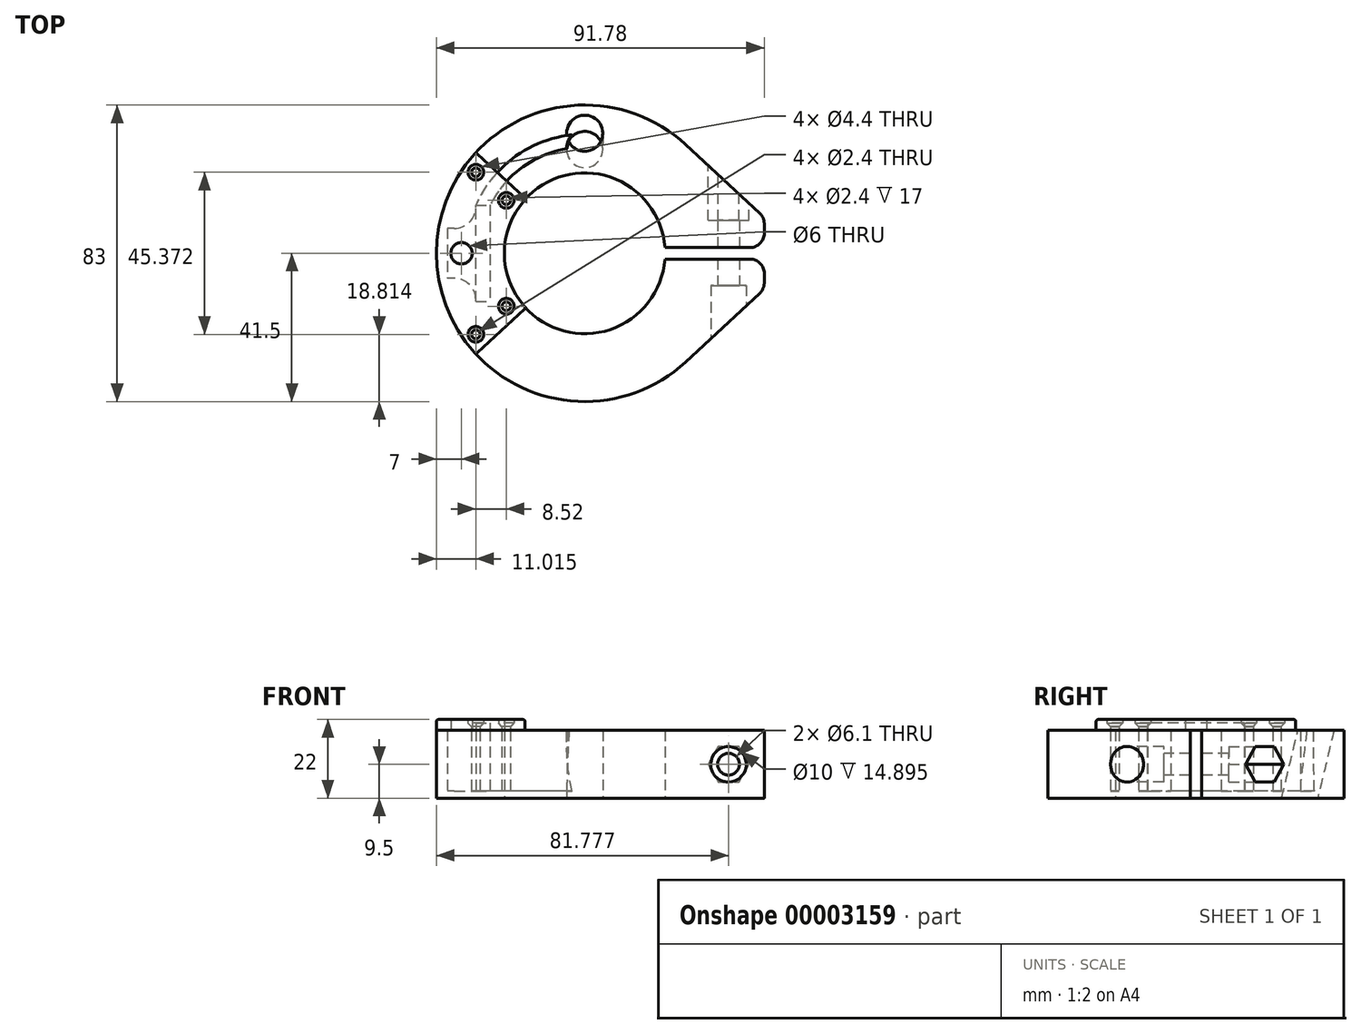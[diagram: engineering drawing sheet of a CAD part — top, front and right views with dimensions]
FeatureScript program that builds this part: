
annotation { "Feature Type Name" : "Feature", "Feature Type Description" : "" }
export const myFeature = defineFeature(function(context is Context, id is Id, definition is map)
    precondition{}
    {
        {
            var Q0;
            Q0=qCreatedBy(makeId("Top.planeOp"),FACE);
            var sketch = newSketch(context, id + "F0", { "sketchPlane" : qUnion([Q0])});
            skCircle(sketch, "E0", {"center": v(0, 0) * mm, "radius": 26.5 * mm, "construction": true});
            skCircle(sketch, "E1", {"center": v(0, 0) * mm, "radius": 38 * mm, "construction": true});
            skLineSegment(sketch, "E2", {"start": v(50.28, 1.6) * mm, "end": v(0, 1.6) * mm});
            skLineSegment(sketch, "E3", {"start": v(0, 1.6) * mm, "end": v(0, -1.6) * mm});
            skLineSegment(sketch, "E4", {"start": v(0, -1.6) * mm, "end": v(50.28, -1.6) * mm});
            skLineSegment(sketch, "E5", {"start": v(40.28, 10) * mm, "end": v(50.28, 10) * mm});
            skLineSegment(sketch, "E6", {"start": v(50.28, 10) * mm, "end": v(50.28, -10) * mm});
            skLineSegment(sketch, "E7", {"start": v(50.28, -10) * mm, "end": v(40.28, -10) * mm});
            skLineSegment(sketch, "E8", {"start": v(-26.5, 13.5) * mm, "end": v(-26.5, -13.5) * mm});
            skLineSegment(sketch, "E9", {"start": v(-30.5, -13.5) * mm, "end": v(-30.5, 13.5) * mm});
            skCircle(sketch, "E10", {"center": v(-34.5, 0) * mm, "radius": 3 * mm});
            skLineSegment(sketch, "E11", {"start": v(-30.5, 0) * mm, "end": v(-26.5, 0) * mm, "construction": true});
            skCircle(sketch, "E12", {"center": v(0, 0) * mm, "radius": 41.5 * mm});
            skLineSegment(sketch, "E13", {"start": v(-30.5, -13.5) * mm, "end": v(-26.5, -13.5) * mm});
            skLineSegment(sketch, "E14", {"start": v(-30.5, 13.5) * mm, "end": v(-26.5, 13.5) * mm});
            skLineSegment(sketch, "E15.rect.bottom", {"start": v(-30.5, 7) * mm, "end": v(-38.5, 7) * mm});
            skLineSegment(sketch, "E15.rect.top", {"start": v(-30.5, -7) * mm, "end": v(-38.5, -7) * mm});
            skLineSegment(sketch, "E15.rect.left", {"start": v(-30.5, 7) * mm, "end": v(-30.5, -7) * mm});
            skLineSegment(sketch, "E15.rect.right", {"start": v(-38.5, 7) * mm, "end": v(-38.5, -7) * mm});
            skCircle(sketch, "E16", {"center": v(0, 28.48) * mm, "radius": 5.05 * mm});
            skLineSegment(sketch, "E17", {"start": v(0, 26.5) * mm, "end": v(0, 41.5) * mm});
            skCircle(sketch, "E18", {"center": v(0, 0) * mm, "radius": 22.5 * mm});
            skLineSegment(sketch, "E19", {"start": v(-26.5, 0) * mm, "end": v(-22.5, 0) * mm});
            skLineSegment(sketch, "E20", {"start": v(0, 0) * mm, "end": v(50.28, 0) * mm, "construction": true});
            skArc(sketch, "E21", {"start": v(-1.43, 33.32) * mm, "mid": v(-18.8, 27.56) * mm, "end": v(-30.5, 13.5) * mm});
            skLineSegment(sketch, "E22", {"start": v(-16.54, 15.26) * mm, "end": v(-30.5, 28.14) * mm});
            skLineSegment(sketch, "E23", {"start": v(-30.5, -28.14) * mm, "end": v(-16.54, -15.26) * mm});
            skLineSegment(sketch, "E24", {"start": v(-30.5, 28.14) * mm, "end": v(-30.5, -28.14) * mm, "construction": true});
            skArc(sketch, "E25.trimOffspring", {"start": v(-4.98, 29.32) * mm, "mid": v(-17.62, 23.96) * mm, "end": v(-26.5, 13.5) * mm});
            skLineSegment(sketch, "E26.0", {"start": v(-33.07, -25.07) * mm, "end": v(-18.99, -12.08) * mm, "construction": true});
            skLineSegment(sketch, "E27.0", {"start": v(-18.99, 12.08) * mm, "end": v(-33.07, 25.07) * mm, "construction": true});
            skCircle(sketch, "E28", {"center": v(-21.97, 14.82) * mm, "radius": 1.2 * mm});
            skCircle(sketch, "E29", {"center": v(-30.49, 22.69) * mm, "radius": 1.2 * mm});
            skCircle(sketch, "E30", {"center": v(-30.49, -22.69) * mm, "radius": 1.2 * mm});
            skCircle(sketch, "E31", {"center": v(-21.97, -14.82) * mm, "radius": 1.2 * mm});
            skLineSegment(sketch, "E32", {"start": v(-38.5, 0) * mm, "end": v(-41.5, 0) * mm, "construction": true});
            skLineSegment(sketch, "E33", {"start": v(0, -38) * mm, "end": v(0, -41.5) * mm, "construction": true});
            skLineSegment(sketch, "E34", {"start": v(50.28, 10) * mm, "end": v(28.2, 30.45) * mm});
            skLineSegment(sketch, "E35", {"start": v(50.28, -10) * mm, "end": v(28.2, -30.45) * mm});
            skCircle(sketch, "E36.0", {"center": v(-30.49, 22.69) * mm, "radius": 2.2 * mm});
            skCircle(sketch, "E37.0", {"center": v(-21.97, 14.82) * mm, "radius": 2.2 * mm});
            skCircle(sketch, "E38.0", {"center": v(-30.49, -22.69) * mm, "radius": 2.2 * mm});
            skCircle(sketch, "E39.0", {"center": v(-21.97, -14.82) * mm, "radius": 2.2 * mm});
            skSolve(sketch);
        }
        {
            var Q0;
            {var subQ13=sQuery(id+"F0.wireOp",EDGE,"E13");Q0=makeQuery(id+"F0.imprint","IMPRINT",FACE,{"disambiguationData":[TD([[makeQuery(id+"F0.imprint","IMPRINT",EDGE,{"derivedFrom":subQ13}),-1.0]])]});}
            var Q1;
            {var subQ7=sQuery(id+"F0.wireOp",EDGE,"E19");Q1=makeQuery(id+"F0.imprint","IMPRINT",FACE,{"disambiguationData":[TD([[makeQuery(id+"F0.imprint","IMPRINT",EDGE,{"derivedFrom":subQ7}),1.0]])]});}
            var Q2;
            {var subQ3=sQuery(id+"F0.wireOp",EDGE,"E14");Q2=makeQuery(id+"F0.imprint","IMPRINT",FACE,{"disambiguationData":[TD([[makeQuery(id+"F0.imprint","IMPRINT",EDGE,{"derivedFrom":subQ3}),1.0]])]});}
            var Q3;
            {var subQ2=sQuery(id+"F0.wireOp",EDGE,"E13");Q3=makeQuery(id+"F0.imprint","IMPRINT",FACE,{"disambiguationData":[TD([[makeQuery(id+"F0.imprint","IMPRINT",EDGE,{"derivedFrom":subQ2}),1.0]])]});}
            var Q4;
            Q4=makeQuery(id+"F0.imprint","IMPRINT",FACE,{"disambiguationData":[TD([[makeQuery(id+"F0.imprint","IMPRINT",EDGE,{"derivedFrom":sQuery(id+"F0.wireOp",EDGE,"E10")}),-1.0]])]});
            extrude(context, id + "F1", {"entities" : qUnion([Q0, Q1, Q2, Q3, Q4]), "depth" : 3 * mm});
        }
        {
            var Q0;
            Q0=makeQuery(id+"F0.imprint","IMPRINT",FACE,{"disambiguationData":[TD([[makeQuery(id+"F0.imprint","IMPRINT",EDGE,{"derivedFrom":sQuery(id+"F0.wireOp",EDGE,"E28")}),-1.0]])]});
            var Q1;
            Q1=makeQuery(id+"F0.imprint","IMPRINT",FACE,{"disambiguationData":[TD([[makeQuery(id+"F0.imprint","IMPRINT",EDGE,{"derivedFrom":sQuery(id+"F0.wireOp",EDGE,"E29")}),-1.0]])]});
            var Q2;
            Q2=makeQuery(id+"F0.imprint","IMPRINT",FACE,{"disambiguationData":[TD([[makeQuery(id+"F0.imprint","IMPRINT",EDGE,{"derivedFrom":sQuery(id+"F0.wireOp",EDGE,"E30")}),-1.0]])]});
            var Q3;
            Q3=makeQuery(id+"F0.imprint","IMPRINT",FACE,{"disambiguationData":[TD([[makeQuery(id+"F0.imprint","IMPRINT",EDGE,{"derivedFrom":sQuery(id+"F0.wireOp",EDGE,"E31")}),-1.0]])]});
            extrude(context, id + "F2", {"entities" : qUnion([Q0, Q1, Q2, Q3]), "operationType" : NewBodyOperationType.ADD, "depth" : 2 * mm});
        }
        {
            var Q0;
            {var subQ2=sQuery(id+"F0.wireOp",EDGE,"E13");Q0=makeQuery(id+"F0.imprint","IMPRINT",FACE,{"disambiguationData":[TD([[makeQuery(id+"F0.imprint","IMPRINT",EDGE,{"derivedFrom":subQ2}),1.0]])]});}
            extrude(context, id + "F3", {"entities" : qUnion([Q0]), "operationType" : NewBodyOperationType.REMOVE, "depth" : 2 * mm});
        }
        {
            var Q0;
            Q0=makeQuery(id+"F1.opExtrude","SWEPT_BODY",BODY,{"disambiguationData":[OSD([sQuery(id+"F0.wireOp",EDGE,"E10"),sQuery(id+"F0.wireOp",EDGE,"E12"),sQuery(id+"F0.wireOp",EDGE,"E18"),sQuery(id+"F0.wireOp",EDGE,"E22"),sQuery(id+"F0.wireOp",EDGE,"E23"),sQuery(id+"F0.wireOp",EDGE,"E36.0"),sQuery(id+"F0.wireOp",EDGE,"E37.0"),sQuery(id+"F0.wireOp",EDGE,"E38.0"),sQuery(id+"F0.wireOp",EDGE,"E39.0")])]});
            transform(context, id + "F4", {"entities" : qUnion([Q0]), "transformType" : TransformType.TRANSLATION_3D, "dx" : 0 * mm, "dy" : 0 * mm, "dz" : 19 * mm, "makeCopy" : false});
        }
        {
            var Q0;
            Q0=makeQuery(id+"F2.opExtrude","CAP_EDGE",EDGE,{"disambiguationData":[OSD([sQuery(id+"F0.wireOp",EDGE,"E30")])],"isStart":false});
            var Q1;
            Q1=makeQuery(id+"F2.opExtrude","CAP_EDGE",EDGE,{"disambiguationData":[OSD([sQuery(id+"F0.wireOp",EDGE,"E31")])],"isStart":false});
            var Q2;
            Q2=makeQuery(id+"F2.opExtrude","CAP_EDGE",EDGE,{"disambiguationData":[OSD([sQuery(id+"F0.wireOp",EDGE,"E28")])],"isStart":false});
            var Q3;
            Q3=makeQuery(id+"F2.opExtrude","CAP_EDGE",EDGE,{"disambiguationData":[OSD([sQuery(id+"F0.wireOp",EDGE,"E29")])],"isStart":false});
            chamfer(context, id + "F5", {"entities" : qUnion([Q0, Q1, Q2, Q3]), "width" : 1 * mm, "tangentPropagation" : true});
        }
        {
            var Q0;
            Q0=makeQuery(id+"F1.opExtrude","CAP_EDGE",EDGE,{"disambiguationData":[OSD([sQuery(id+"F0.wireOp",EDGE,"E23")])],"isStart":false});
            var Q1;
            Q1=makeQuery(id+"F1.opExtrude","CAP_EDGE",EDGE,{"disambiguationData":[OSD([sQuery(id+"F0.wireOp",EDGE,"E22")])],"isStart":false});
            var Q2;
            Q2=makeQuery(id+"F1.opExtrude","CAP_EDGE",EDGE,{"disambiguationData":[OSD([sQuery(id+"F0.wireOp",EDGE,"E18")])],"isStart":false});
            var Q3;
            Q3=makeQuery(id+"F1.opExtrude","CAP_EDGE",EDGE,{"disambiguationData":[OSD([sQuery(id+"F0.wireOp",EDGE,"E12")])],"isStart":false});
            var Q4;
            Q4=makeQuery(id+"F1.opExtrude","SWEPT_EDGE",EDGE,{"disambiguationData":[OSD([sQuery(id+"F0.wireOp",EDGE,"E12"),sQuery(id+"F0.wireOp",EDGE,"E23")])]});
            var Q5;
            Q5=makeQuery(id+"F1.opExtrude","SWEPT_EDGE",EDGE,{"disambiguationData":[OSD([sQuery(id+"F0.wireOp",EDGE,"E18"),sQuery(id+"F0.wireOp",EDGE,"E23")])]});
            var Q6;
            Q6=makeQuery(id+"F1.opExtrude","SWEPT_EDGE",EDGE,{"disambiguationData":[OSD([sQuery(id+"F0.wireOp",EDGE,"E12"),sQuery(id+"F0.wireOp",EDGE,"E22")])]});
            var Q7;
            Q7=makeQuery(id+"F1.opExtrude","SWEPT_EDGE",EDGE,{"disambiguationData":[OSD([sQuery(id+"F0.wireOp",EDGE,"E18"),sQuery(id+"F0.wireOp",EDGE,"E22")])]});
            fillet(context, id + "F6", {"entities" : qUnion([Q0, Q1, Q2, Q3, Q4, Q5, Q6, Q7]), "radius" : .5 * mm, "tangentPropagation" : true, "allowEdgeOverflow" : false});
        }
        {
            var Q0;
            {var subQ13=sQuery(id+"F0.wireOp",EDGE,"E13");Q0=makeQuery(id+"F0.imprint","IMPRINT",FACE,{"disambiguationData":[TD([[makeQuery(id+"F0.imprint","IMPRINT",EDGE,{"derivedFrom":subQ13}),-1.0]])]});}
            var Q1;
            {var subQ3=sQuery(id+"F0.wireOp",EDGE,"E5");Q1=makeQuery(id+"F0.imprint","IMPRINT",FACE,{"disambiguationData":[TD([[makeQuery(id+"F0.imprint","IMPRINT",EDGE,{"derivedFrom":subQ3}),-1.0]])]});}
            var Q2;
            {var subQ3=sQuery(id+"F0.wireOp",EDGE,"E7");Q2=makeQuery(id+"F0.imprint","IMPRINT",FACE,{"disambiguationData":[TD([[makeQuery(id+"F0.imprint","IMPRINT",EDGE,{"derivedFrom":subQ3}),-1.0]])]});}
            var Q3;
            {var subQ0=sQuery(id+"F0.wireOp",EDGE,"E23");Q3=makeQuery(id+"F0.imprint","IMPRINT",FACE,{"disambiguationData":[TD([[makeQuery(id+"F0.imprint","IMPRINT",EDGE,{"derivedFrom":subQ0}),-1.0]])]});}
            var Q4;
            {var subQ3=sQuery(id+"F0.wireOp",EDGE,"E12");var subQ7=sQuery(id+"F0.wireOp",EDGE,"E17");var subQ9=makeQuery(id+"F0.imprint","INTERSECT",VERTEX,{"derivedFrom":[subQ3,subQ7]});Q4=makeQuery(id+"F0.imprint","IMPRINT",FACE,{"disambiguationData":[TD([[makeQuery(id+"F0.imprint","IMPRINT",EDGE,{"disambiguationData":[TD([[subQ9,-1.0]])],"derivedFrom":subQ3}),1.0]])]});}
            var Q5;
            {var subQ7=sQuery(id+"F0.wireOp",EDGE,"E19");Q5=makeQuery(id+"F0.imprint","IMPRINT",FACE,{"disambiguationData":[TD([[makeQuery(id+"F0.imprint","IMPRINT",EDGE,{"derivedFrom":subQ7}),1.0]])]});}
            var Q6;
            {var subQ9=sQuery(id+"F0.wireOp",EDGE,"E17");Q6=makeQuery(id+"F0.imprint","IMPRINT",FACE,{"disambiguationData":[TD([[makeQuery(id+"F0.imprint","IMPRINT",EDGE,{"disambiguationData":[TD([[makeQuery(id+"F0.imprint","IMPRINT",VERTEX,{"derivedFrom":sQuery(id+"F0.wireOp",VERTEX,"E17.start")}),-1.0]])],"derivedFrom":subQ9}),1.0]])]});}
            var Q7;
            {var subQ0=sQuery(id+"F0.wireOp",EDGE,"E17");var subQ1=sQuery(id+"F0.wireOp",EDGE,"E16");var subQ3=makeQuery(id+"F0.imprint","INTERSECT",VERTEX,{"disambiguationData":[OD(0.0)],"derivedFrom":[subQ1,subQ0]});Q7=makeQuery(id+"F0.imprint","IMPRINT",FACE,{"disambiguationData":[TD([[makeQuery(id+"F0.imprint","IMPRINT",EDGE,{"disambiguationData":[TD([[subQ3,-1.0]])],"derivedFrom":subQ1}),1.0]])]});}
            var Q8;
            {var subQ1=sQuery(id+"F0.wireOp",EDGE,"E16");var subQ5=makeQuery(id+"F0.imprint","INTERSECT",VERTEX,{"derivedFrom":[subQ1,sQuery(id+"F0.wireOp",EDGE,"E21")]});Q8=makeQuery(id+"F0.imprint","IMPRINT",FACE,{"disambiguationData":[TD([[makeQuery(id+"F0.imprint","IMPRINT",EDGE,{"disambiguationData":[TD([[subQ5,1.0]])],"derivedFrom":subQ1}),1.0]])]});}
            var Q9;
            Q9=makeQuery(id+"F0.imprint","IMPRINT",FACE,{"disambiguationData":[TD([[makeQuery(id+"F0.imprint","IMPRINT",EDGE,{"derivedFrom":sQuery(id+"F0.wireOp",EDGE,"E30")}),-1.0]])]});
            var Q10;
            Q10=makeQuery(id+"F0.imprint","IMPRINT",FACE,{"disambiguationData":[TD([[makeQuery(id+"F0.imprint","IMPRINT",EDGE,{"derivedFrom":sQuery(id+"F0.wireOp",EDGE,"E31")}),-1.0]])]});
            var Q11;
            Q11=makeQuery(id+"F0.imprint","IMPRINT",FACE,{"disambiguationData":[TD([[makeQuery(id+"F0.imprint","IMPRINT",EDGE,{"derivedFrom":sQuery(id+"F0.wireOp",EDGE,"E29")}),-1.0]])]});
            var Q12;
            Q12=makeQuery(id+"F0.imprint","IMPRINT",FACE,{"disambiguationData":[TD([[makeQuery(id+"F0.imprint","IMPRINT",EDGE,{"derivedFrom":sQuery(id+"F0.wireOp",EDGE,"E28")}),-1.0]])]});
            var Q13;
            {var subQ1=sQuery(id+"F0.wireOp",EDGE,"E12");var subQ5=sQuery(id+"F0.wireOp",EDGE,"E2");var subQ6=makeQuery(id+"F0.imprint","INTERSECT",VERTEX,{"derivedFrom":[subQ5,subQ1]});Q13=makeQuery(id+"F0.imprint","IMPRINT",FACE,{"disambiguationData":[TD([[makeQuery(id+"F0.imprint","IMPRINT",EDGE,{"disambiguationData":[TD([[subQ6,-1.0]])],"derivedFrom":subQ5}),-1.0]])]});}
            extrude(context, id + "F7", {"entities" : qUnion([Q0, Q1, Q2, Q3, Q4, Q5, Q6, Q7, Q8, Q9, Q10, Q11, Q12, Q13]), "depth" : 19 * mm});
        }
        {
            var Q0;
            {var subQ2=sQuery(id+"F0.wireOp",EDGE,"E13");Q0=makeQuery(id+"F0.imprint","IMPRINT",FACE,{"disambiguationData":[TD([[makeQuery(id+"F0.imprint","IMPRINT",EDGE,{"derivedFrom":subQ2}),1.0]])]});}
            var Q1;
            {var subQ3=sQuery(id+"F0.wireOp",EDGE,"E14");Q1=makeQuery(id+"F0.imprint","IMPRINT",FACE,{"disambiguationData":[TD([[makeQuery(id+"F0.imprint","IMPRINT",EDGE,{"derivedFrom":subQ3}),1.0]])]});}
            var Q2;
            {var subQ3=sQuery(id+"F0.wireOp",EDGE,"E16");var subQ5=sQuery(id+"F0.wireOp",EDGE,"E21");var subQ7=makeQuery(id+"F0.imprint","INTERSECT",VERTEX,{"derivedFrom":[subQ3,subQ5]});Q2=makeQuery(id+"F0.imprint","IMPRINT",FACE,{"disambiguationData":[TD([[makeQuery(id+"F0.imprint","IMPRINT",EDGE,{"disambiguationData":[TD([[subQ7,-1.0]])],"derivedFrom":subQ3}),-1.0]])]});}
            var Q3;
            Q3=makeQuery(id+"F0.imprint","IMPRINT",FACE,{"disambiguationData":[TD([[makeQuery(id+"F0.imprint","IMPRINT",EDGE,{"derivedFrom":sQuery(id+"F0.wireOp",EDGE,"E10")}),-1.0]])]});
            var Q4;
            Q4=makeQuery(id+"F0.imprint","IMPRINT",FACE,{"disambiguationData":[TD([[makeQuery(id+"F0.imprint","IMPRINT",EDGE,{"derivedFrom":sQuery(id+"F0.wireOp",EDGE,"E10")}),1.0]])]});
            extrude(context, id + "F8", {"entities" : qUnion([Q0, Q1, Q2, Q3, Q4]), "operationType" : NewBodyOperationType.ADD, "depth" : 2 * mm});
        }
        {
            var Q0;
            {var subQ2=sQuery(id+"F0.wireOp",EDGE,"E13");Q0=makeQuery(id+"F0.imprint","IMPRINT",FACE,{"disambiguationData":[TD([[makeQuery(id+"F0.imprint","IMPRINT",EDGE,{"derivedFrom":subQ2}),1.0]])]});}
            extrude(context, id + "F9", {"entities" : qUnion([Q0]), "operationType" : NewBodyOperationType.ADD, "depth" : 1 * mm});
        }
        {
            var Q0;
            Q0=makeQuery(id+"F0.imprint","IMPRINT",FACE,{"disambiguationData":[TD([[makeQuery(id+"F0.imprint","IMPRINT",EDGE,{"derivedFrom":sQuery(id+"F0.wireOp",EDGE,"E31")}),1.0]])]});
            var Q1;
            Q1=makeQuery(id+"F0.imprint","IMPRINT",FACE,{"disambiguationData":[TD([[makeQuery(id+"F0.imprint","IMPRINT",EDGE,{"derivedFrom":sQuery(id+"F0.wireOp",EDGE,"E30")}),1.0]])]});
            var Q2;
            Q2=makeQuery(id+"F0.imprint","IMPRINT",FACE,{"disambiguationData":[TD([[makeQuery(id+"F0.imprint","IMPRINT",EDGE,{"derivedFrom":sQuery(id+"F0.wireOp",EDGE,"E28")}),1.0]])]});
            var Q3;
            Q3=makeQuery(id+"F0.imprint","IMPRINT",FACE,{"disambiguationData":[TD([[makeQuery(id+"F0.imprint","IMPRINT",EDGE,{"derivedFrom":sQuery(id+"F0.wireOp",EDGE,"E29")}),1.0]])]});
            extrude(context, id + "F10", {"entities" : qUnion([Q0, Q1, Q2, Q3]), "operationType" : NewBodyOperationType.ADD, "depth" : 2 * mm});
        }
        {
            var Q0;
            Q0=makeQuery(id+"F7.opExtrude","SWEPT_EDGE",EDGE,{"disambiguationData":[OSD([sQuery(id+"F0.wireOp",EDGE,"E9"),sQuery(id+"F0.wireOp",EDGE,"E15.rect.bottom"),sQuery(id+"F0.wireOp",EDGE,"E15.rect.left")])]});
            var Q1;
            Q1=makeQuery(id+"F7.opExtrude","SWEPT_EDGE",EDGE,{"disambiguationData":[OSD([sQuery(id+"F0.wireOp",EDGE,"E9"),sQuery(id+"F0.wireOp",EDGE,"E15.rect.top"),sQuery(id+"F0.wireOp",EDGE,"E15.rect.left")])]});
            fillet(context, id + "F11", {"entities" : qUnion([Q0, Q1]), "radius" : 6 * mm, "tangentPropagation" : true, "allowEdgeOverflow" : false});
        }
        {
            var Q0;
            Q0=makeQuery(id+"F7.opExtrude","SWEPT_FACE",FACE,{"disambiguationData":[OSD([sQuery(id+"F0.wireOp",EDGE,"E7")])]});
            var sketch = newSketch(context, id + "F12", { "sketchPlane" : qUnion([Q0])});
            skCircle(sketch, "E40", {"center": v(40.28, 9.5) * mm, "radius": 3.05 * mm});
            skSolve(sketch);
        }
        {
            var Q0;
            {var subQ2=sQuery(id+"F0.wireOp",EDGE,"E7");Q0=makeQuery(id+"F0.imprint","IMPRINT",FACE,{"disambiguationData":[TD([[makeQuery(id+"F0.imprint","IMPRINT",EDGE,{"derivedFrom":subQ2}),1.0]])]});}
            var Q1;
            {var subQ2=sQuery(id+"F0.wireOp",EDGE,"E5");Q1=makeQuery(id+"F0.imprint","IMPRINT",FACE,{"disambiguationData":[TD([[makeQuery(id+"F0.imprint","IMPRINT",EDGE,{"derivedFrom":subQ2}),1.0]])]});}
            extrude(context, id + "F13", {"entities" : qUnion([Q0, Q1]), "operationType" : NewBodyOperationType.ADD, "depth" : 19 * mm});
        }
        {
            var Q0;
            {var subQ0=makeQuery(id+"F7.opExtrude","SWEPT_EDGE",EDGE,{"disambiguationData":[OSD([sQuery(id+"F0.wireOp",EDGE,"E7"),sQuery(id+"F0.wireOp",EDGE,"E12")])]});var subQ1=sQuery(id+"F12.wireOp",EDGE,"E40");var subQ3=makeQuery(id+"F12.imprint","INTERSECT",VERTEX,{"disambiguationData":[OD(0.0)],"derivedFrom":[subQ0,subQ1]});Q0=qUnion([makeQuery(id+"F12.imprint","IMPRINT",FACE,{"disambiguationData":[TD([[makeQuery(id+"F12.imprint","IMPRINT",EDGE,{"disambiguationData":[TD([[subQ3,1.0]])],"derivedFrom":subQ1}),1.0]])]}),makeQuery(id+"F12.imprint","IMPRINT",FACE,{"disambiguationData":[TD([[makeQuery(id+"F12.imprint","IMPRINT",EDGE,{"disambiguationData":[TD([[subQ3,-1.0]])],"derivedFrom":subQ1}),1.0]])]})]);}
            extrude(context, id + "F14", {"entities" : qUnion([Q0]), "operationType" : NewBodyOperationType.REMOVE, "endBound" : BoundingType.SYMMETRIC, "oppositeDirection" : true, "depth" : 100 * mm});
        }
        {
            var Q0;
            {var subQ0=sQuery(id+"F0.wireOp",EDGE,"E6");var subQ1=sQuery(id+"F0.wireOp",EDGE,"E7");var subQ2=sQuery(id+"F0.wireOp",EDGE,"E35");Q0=makeQuery(id+"F13.boolean.opBoolean","MERGE",EDGE,{"derivedFrom":[makeQuery(id+"F7.opExtrude","SWEPT_EDGE",EDGE,{"disambiguationData":[OSD([subQ0,subQ1,subQ2])]}),makeQuery(id+"F13.opExtrude","SWEPT_EDGE",EDGE,{"disambiguationData":[OSD([subQ0,subQ1,subQ2])]})]});}
            var Q1;
            {var subQ0=sQuery(id+"F0.wireOp",EDGE,"E5");var subQ1=sQuery(id+"F0.wireOp",EDGE,"E6");var subQ2=sQuery(id+"F0.wireOp",EDGE,"E34");Q1=makeQuery(id+"F13.boolean.opBoolean","MERGE",EDGE,{"derivedFrom":[makeQuery(id+"F7.opExtrude","SWEPT_EDGE",EDGE,{"disambiguationData":[OSD([subQ0,subQ1,subQ2])]}),makeQuery(id+"F13.opExtrude","SWEPT_EDGE",EDGE,{"disambiguationData":[OSD([subQ0,subQ1,subQ2])]})]});}
            var Q2;
            Q2=makeQuery(id+"F7.opExtrude","SWEPT_EDGE",EDGE,{"disambiguationData":[OSD([sQuery(id+"F0.wireOp",EDGE,"E2"),sQuery(id+"F0.wireOp",EDGE,"E6")])]});
            var Q3;
            Q3=makeQuery(id+"F7.opExtrude","SWEPT_EDGE",EDGE,{"disambiguationData":[OSD([sQuery(id+"F0.wireOp",EDGE,"E4"),sQuery(id+"F0.wireOp",EDGE,"E6")])]});
            fillet(context, id + "F15", {"entities" : qUnion([Q0, Q1, Q2, Q3]), "radius" : 4 * mm, "tangentPropagation" : true, "allowEdgeOverflow" : false});
        }
        {
            var Q0;
            Q0=qCreatedBy(makeId("Front.planeOp"),FACE);
            cPlane(context, id + "F16", {"entities" : qUnion([Q0]), "cplaneType" : CPlaneType.OFFSET, "offset" : 27 * mm, "oppositeDirection" : true, "width" : 150 * mm, "height" : 150 * mm});
        }
        {
            var Q0;
            Q0=qCreatedBy(id+"F16.planeOp",FACE);
            var sketch = newSketch(context, id + "F17", { "sketchPlane" : qUnion([Q0])});
            skCircle(sketch, "E41.1", {"center": v(40.28, 9.5) * mm, "radius": 3.05 * mm});
            skCircle(sketch, "E42.cCircle", {"center": v(40.28, 9.5) * mm, "radius": 5 * mm, "construction": true});
            skLineSegment(sketch, "E42.0", {"start": v(43.16, 14.5) * mm, "end": v(46.05, 9.5) * mm});
            skLineSegment(sketch, "E42.1", {"start": v(46.05, 9.5) * mm, "end": v(43.16, 4.5) * mm});
            skLineSegment(sketch, "E42.2", {"start": v(43.16, 4.5) * mm, "end": v(37.4, 4.5) * mm});
            skLineSegment(sketch, "E42.3", {"start": v(37.4, 4.5) * mm, "end": v(34.5, 9.5) * mm});
            skLineSegment(sketch, "E42.4", {"start": v(34.5, 9.5) * mm, "end": v(37.4, 14.5) * mm});
            skLineSegment(sketch, "E42.5", {"start": v(37.4, 14.5) * mm, "end": v(43.16, 14.5) * mm});
            skPoint(sketch, "E42.0.midPoint", {"position": v(44.6, 12) * mm});
            skSolve(sketch);
        }
        {
            var Q0;
            Q0=makeQuery(id+"F17.imprint","IMPRINT",FACE,{"disambiguationData":[TD([[makeQuery(id+"F17.imprint","IMPRINT",EDGE,{"derivedFrom":sQuery(id+"F17.wireOp",EDGE,"E41.1")}),-1.0]])]});
            extrude(context, id + "F18", {"entities" : qUnion([Q0]), "operationType" : NewBodyOperationType.REMOVE, "depth" : 17.8 * mm});
        }
        {
            var Q0;
            Q0=qCreatedBy(makeId("Front.planeOp"),FACE);
            cPlane(context, id + "F19", {"entities" : qUnion([Q0]), "cplaneType" : CPlaneType.OFFSET, "offset" : 27 * mm, "width" : 150 * mm, "height" : 150 * mm});
        }
        {
            var Q0;
            Q0=qCreatedBy(id+"F19.planeOp",FACE);
            var sketch = newSketch(context, id + "F20", { "sketchPlane" : qUnion([Q0])});
            skCircle(sketch, "E43.0", {"center": v(40.28, 9.5) * mm, "radius": 3.05 * mm});
            skCircle(sketch, "E44", {"center": v(40.28, 9.5) * mm, "radius": 5 * mm});
            skSolve(sketch);
        }
        {
            var Q0;
            Q0=makeQuery(id+"F20.imprint","IMPRINT",FACE,{"disambiguationData":[TD([[makeQuery(id+"F20.imprint","IMPRINT",EDGE,{"derivedFrom":sQuery(id+"F20.wireOp",EDGE,"E43.0")}),-1.0]])]});
            extrude(context, id + "F21", {"entities" : qUnion([Q0]), "operationType" : NewBodyOperationType.REMOVE, "oppositeDirection" : true, "depth" : 18 * mm});
        }
        {
            var Q0;
            Q0=qCreatedBy(makeId("Right.planeOp"),FACE);
            var sketch = newSketch(context, id + "F22", { "sketchPlane" : qUnion([Q0])});
            skLineSegment(sketch, "E45", {"start": v(0, 0) * mm, "end": v(0, -121) * mm});
            skLineSegment(sketch, "E46", {"start": v(0, -121) * mm, "end": v(64.79, 148.86) * mm});
            skSolve(sketch);
        }
        {
            var Q0;
            Q0=qCreatedBy(makeId("Top.planeOp"),FACE);
            cPlane(context, id + "F23", {"entities" : qUnion([Q0]), "cplaneType" : CPlaneType.OFFSET, "offset" : 121 * mm, "oppositeDirection" : true, "width" : 150 * mm, "height" : 150 * mm});
        }
        {
            var Q0;
            Q0=qCreatedBy(id+"F23.planeOp",FACE);
            var sketch = newSketch(context, id + "F24", { "sketchPlane" : qUnion([Q0])});
            skCircle(sketch, "E47", {"center": v(0, 0) * mm, "radius": 5.05 * mm});
            skCircle(sketch, "E48.0", {"center": v(0, 28.48) * mm, "radius": 5.05 * mm});
            skSolve(sketch);
        }
        {
            var Q0;
            Q0=makeQuery(id+"F24.imprint","IMPRINT",FACE,{"disambiguationData":[TD([[makeQuery(id+"F24.imprint","IMPRINT",EDGE,{"derivedFrom":sQuery(id+"F24.wireOp",EDGE,"E47")}),1.0]])]});
            var Q1;
            Q1=sQuery(id+"F22.wireOp",EDGE,"E46");
            sweep(context, id + "F25", {"operationType" : NewBodyOperationType.REMOVE, "profiles" : qUnion([Q0]), "path" : qUnion([Q1])});
        }
    });
